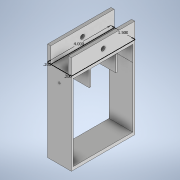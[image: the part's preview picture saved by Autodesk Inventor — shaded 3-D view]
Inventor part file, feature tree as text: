
AUTODESK INVENTOR PART (.ipt)
format: ipt  version: 2020 (Build 240168000, 168)  size: 202,752 bytes
history: native  units: in
note: dims shown in document units (in); Inventor stores cm internally (conversion verified against a paired STEP export)
features: sketch x5, extrude x5, hole x2, fillet x1
ambient origin geometry x8: Origin, YZ Plane, XZ Plane, XY Plane, X Axis, Y Axis, Z Axis, Center Point
bodies: Solid1 (feature_tree)
feature tree (13):
  sketch  "Sketch1"  dims[d0=1.5in d1=4.0in]
  extrude  "Extrusion1"  Depth=4.0in
  extrude  "Extrusion2"  Depth=0.2in
  hole  "Hole1"  [1 undecoded]
  extrude  "Extrusion3"  Depth=3.8in
  hole  "Hole2"  [1 undecoded]
  extrude  "Extrusion4"  Depth=3.8in
  extrude  "Extrusion5"  Depth=0.125in
  fillet  "Fillet1"  Radius=0.125in
  sketch  "Sketch2"  dims[d2=0.2in d3=0.2in]
  sketch  "Sketch3"  dims[d4=1.0in d5=0.0in d6=0.2in d7=0.0in]
  sketch  "Sketch5"  dims[d8=0.5in]
  sketch  "Sketch6"  dims[d9=0.266in d10=0.75in d11=0.438in d12=0.25in d13=0.5635in d14=1.0in d15=0.8108in d16=0.5in d17=1.0in d18=0.75in d19=0.125in d20=0.125in d21=1.0in d22=0.0in d23=0.45in d24=0.1125in d25=0.75in d26=0.438in d27=0.25in d28=0.5635in d29=1.0in d30=0.8108in d31=0.125in d32=0.125in d33=0.125in d34=1.0in d35=1.0in d36=90.0deg d37=0.1in d38=0.1in d39=4.0in d40=0.0in d41=0.2in d42=3.8in d43=0.0in]
note: 2 required parameter values undecoded (feature->parameter linkage not recoverable at this tier; creation-order binding heuristic only, values carry confidence <= 0.55)
